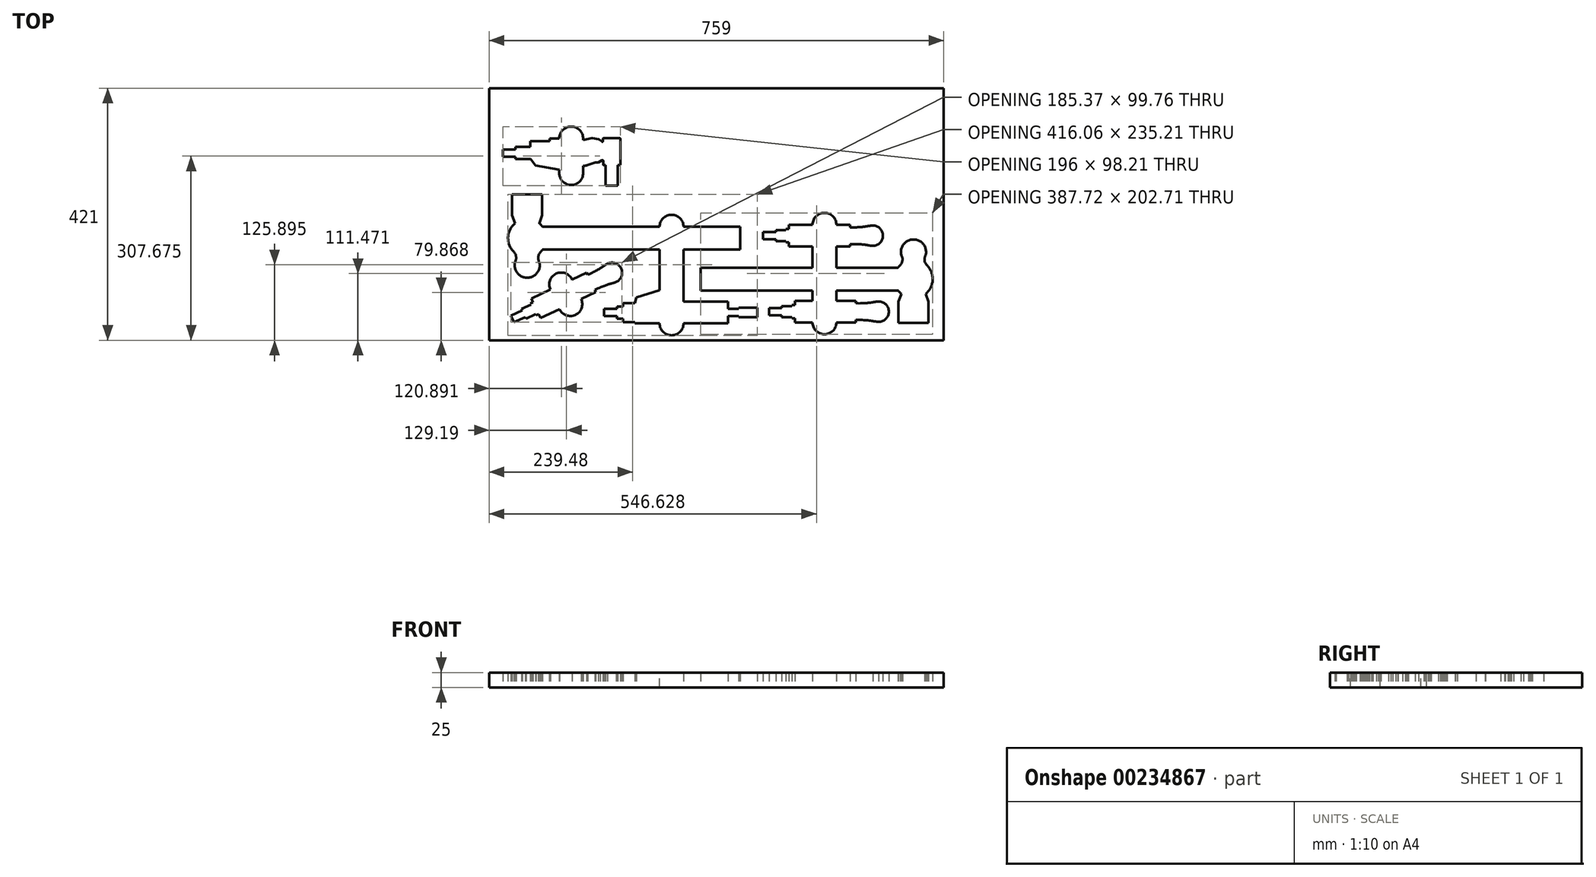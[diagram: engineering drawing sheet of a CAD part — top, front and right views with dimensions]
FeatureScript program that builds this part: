
annotation { "Feature Type Name" : "Feature", "Feature Type Description" : "" }
export const myFeature = defineFeature(function(context is Context, id is Id, definition is map)
    precondition{}
    {
        {
            var Q0;
            Q0=qCreatedBy(makeId("Top.planeOp"),FACE);
            var sketch = newSketch(context, id + "F0", { "sketchPlane" : qUnion([Q0])});
            skLineSegment(sketch, "E0.bottom", {"start": v(0, 0) * mm, "end": v(759, 0) * mm});
            skLineSegment(sketch, "E0.top", {"start": v(0, 421) * mm, "end": v(759, 421) * mm});
            skLineSegment(sketch, "E0.left", {"start": v(0, 0) * mm, "end": v(0, 421) * mm});
            skLineSegment(sketch, "E0.right", {"start": v(759, 0) * mm, "end": v(759, 421) * mm});
            skLineSegment(sketch, "E1", {"start": v(352.77, 83.32) * mm, "end": v(682.77, 83.32) * mm});
            skLineSegment(sketch, "E2", {"start": v(352.77, 83.32) * mm, "end": v(352.77, 121.32) * mm});
            skLineSegment(sketch, "E3", {"start": v(352.77, 121.32) * mm, "end": v(682.77, 121.32) * mm});
            skCircle(sketch, "E4", {"center": v(708.52, 102.32) * mm, "radius": 32 * mm, "construction": true});
            skPoint(sketch, "E4.third.point", {"position": v(740.52, 102.32) * mm});
            skArc(sketch, "E5", {"start": v(728.91, 142.32) * mm, "mid": v(708.52, 168.32) * mm, "end": v(688.12, 142.32) * mm, "construction": true});
            skArc(sketch, "E6", {"start": v(688.12, 142.32) * mm, "mid": v(690.06, 133.5) * mm, "end": v(686.27, 125.32) * mm});
            skArc(sketch, "E7", {"start": v(728.91, 142.32) * mm, "mid": v(726.97, 133.5) * mm, "end": v(730.77, 125.32) * mm});
            skArc(sketch, "E8", {"start": v(688.12, 142.32) * mm, "mid": v(708.52, 168.32) * mm, "end": v(728.91, 142.32) * mm});
            skArc(sketch, "E9", {"start": v(682.77, 121.32) * mm, "mid": v(684.43, 123.4) * mm, "end": v(686.27, 125.32) * mm});
            skArc(sketch, "E10", {"start": v(730.77, 125.32) * mm, "mid": v(740.52, 102.32) * mm, "end": v(730.77, 79.32) * mm});
            skLineSegment(sketch, "E11", {"start": v(688.31, 77.5) * mm, "end": v(683.52, 64.32) * mm});
            skLineSegment(sketch, "E12", {"start": v(728.72, 77.5) * mm, "end": v(733.52, 64.32) * mm});
            skLineSegment(sketch, "E13", {"start": v(733.52, 64.32) * mm, "end": v(733.52, 29.32) * mm});
            skLineSegment(sketch, "E14", {"start": v(733.52, 29.32) * mm, "end": v(683.52, 29.32) * mm});
            skLineSegment(sketch, "E15", {"start": v(683.52, 29.32) * mm, "end": v(683.52, 64.32) * mm});
            skLineSegment(sketch, "E16", {"start": v(683.52, 64.32) * mm, "end": v(733.52, 64.32) * mm, "construction": true});
            skArc(sketch, "E17", {"start": v(682.77, 83.32) * mm, "mid": v(685.36, 80.24) * mm, "end": v(688.31, 77.5) * mm});
            skArc(sketch, "E18", {"start": v(728.72, 77.5) * mm, "mid": v(729.76, 78.39) * mm, "end": v(730.77, 79.32) * mm});
            skLineSegment(sketch, "E19", {"start": v(419.17, 189.5) * mm, "end": v(89.17, 189.5) * mm});
            skLineSegment(sketch, "E20", {"start": v(419.17, 189.5) * mm, "end": v(419.17, 151.5) * mm});
            skLineSegment(sketch, "E21", {"start": v(419.17, 151.5) * mm, "end": v(89.17, 151.5) * mm});
            skCircle(sketch, "E22", {"center": v(63.42, 170.5) * mm, "radius": 32 * mm, "construction": true});
            skPoint(sketch, "E22.third.point", {"position": v(31.42, 170.5) * mm});
            skArc(sketch, "E23", {"start": v(43.02, 130.5) * mm, "mid": v(63.42, 104.5) * mm, "end": v(83.82, 130.5) * mm, "construction": true});
            skArc(sketch, "E24", {"start": v(83.82, 130.5) * mm, "mid": v(81.88, 139.31) * mm, "end": v(85.67, 147.5) * mm});
            skArc(sketch, "E25", {"start": v(43.02, 130.5) * mm, "mid": v(44.96, 139.31) * mm, "end": v(41.17, 147.5) * mm});
            skArc(sketch, "E26", {"start": v(83.82, 130.5) * mm, "mid": v(63.42, 104.5) * mm, "end": v(43.02, 130.5) * mm});
            skArc(sketch, "E27", {"start": v(89.17, 151.5) * mm, "mid": v(87.5, 149.43) * mm, "end": v(85.67, 147.5) * mm});
            skArc(sketch, "E28", {"start": v(41.17, 147.5) * mm, "mid": v(31.42, 170.5) * mm, "end": v(41.17, 193.5) * mm});
            skLineSegment(sketch, "E29", {"start": v(83.62, 195.32) * mm, "end": v(88.42, 208.5) * mm});
            skLineSegment(sketch, "E30", {"start": v(43.22, 195.32) * mm, "end": v(38.42, 208.5) * mm});
            skLineSegment(sketch, "E31", {"start": v(38.42, 208.5) * mm, "end": v(38.42, 243.5) * mm});
            skLineSegment(sketch, "E32", {"start": v(38.42, 243.5) * mm, "end": v(88.42, 243.5) * mm});
            skLineSegment(sketch, "E33", {"start": v(88.42, 243.5) * mm, "end": v(88.42, 208.5) * mm});
            skLineSegment(sketch, "E34", {"start": v(88.42, 208.5) * mm, "end": v(38.42, 208.5) * mm, "construction": true});
            skArc(sketch, "E35", {"start": v(89.17, 189.5) * mm, "mid": v(86.58, 192.58) * mm, "end": v(83.62, 195.32) * mm});
            skArc(sketch, "E36", {"start": v(43.22, 195.32) * mm, "mid": v(42.18, 194.43) * mm, "end": v(41.17, 193.5) * mm});
            skLineSegment(sketch, "E37", {"start": v(467.27, 47.8) * mm, "end": v(650.27, 47.8) * mm, "construction": true});
            skLineSegment(sketch, "E38", {"start": v(467.27, 47.8) * mm, "end": v(467.27, 41.8) * mm});
            skLineSegment(sketch, "E39", {"start": v(467.27, 41.8) * mm, "end": v(488.27, 41.8) * mm});
            skLineSegment(sketch, "E40", {"start": v(488.27, 41.8) * mm, "end": v(488.27, 38.8) * mm});
            skLineSegment(sketch, "E41", {"start": v(488.27, 38.8) * mm, "end": v(505.27, 38.8) * mm});
            skLineSegment(sketch, "E42", {"start": v(505.27, 38.8) * mm, "end": v(505.27, 36.8) * mm});
            skLineSegment(sketch, "E43", {"start": v(505.27, 36.8) * mm, "end": v(510.27, 36.8) * mm});
            skLineSegment(sketch, "E44", {"start": v(510.27, 36.8) * mm, "end": v(510.27, 29.8) * mm});
            skLineSegment(sketch, "E45", {"start": v(510.27, 29.8) * mm, "end": v(612.27, 29.8) * mm});
            skLineSegment(sketch, "E46", {"start": v(612.27, 29.8) * mm, "end": v(612.27, 33.8) * mm});
            skFitSpline(sketch, "E47", {"points": [v(612.27, 33.8) * mm, v(650.27, 30.8) * mm], "startDerivative": vector(70.31, 1.78) * mm, "endDerivative": vector(28.37, -1.58) * mm});
            skArc(sketch, "E48", {"start": v(650.27, 30.8) * mm, "mid": v(667.27, 47.8) * mm, "end": v(650.27, 64.8) * mm});
            skLineSegment(sketch, "E49.MirrorCS", {"start": v(510.27, 65.8) * mm, "end": v(612.27, 65.8) * mm});
            skLineSegment(sketch, "E50.MirrorCS", {"start": v(612.27, 65.8) * mm, "end": v(612.27, 61.8) * mm});
            skFitSpline(sketch, "E51.MirrorCS", {"points": [v(612.27, 61.8) * mm, v(650.27, 64.8) * mm], "startDerivative": vector(70.31, -1.78) * mm, "endDerivative": vector(28.37, 1.58) * mm});
            skLineSegment(sketch, "E52.MirrorCS", {"start": v(505.27, 58.8) * mm, "end": v(510.27, 58.8) * mm});
            skLineSegment(sketch, "E53.MirrorCS", {"start": v(510.27, 58.8) * mm, "end": v(510.27, 65.8) * mm});
            skLineSegment(sketch, "E54.MirrorCS", {"start": v(488.27, 56.8) * mm, "end": v(505.27, 56.8) * mm});
            skLineSegment(sketch, "E55.MirrorCS", {"start": v(505.27, 56.8) * mm, "end": v(505.27, 58.8) * mm});
            skLineSegment(sketch, "E56.MirrorCS", {"start": v(488.27, 53.8) * mm, "end": v(488.27, 56.8) * mm});
            skLineSegment(sketch, "E57.MirrorCS", {"start": v(467.27, 53.8) * mm, "end": v(488.27, 53.8) * mm});
            skLineSegment(sketch, "E58.MirrorCS", {"start": v(467.27, 47.8) * mm, "end": v(467.27, 53.8) * mm});
            skLineSegment(sketch, "E59", {"start": v(39.04, 35.43) * mm, "end": v(204.9, 112.76) * mm, "construction": true});
            skLineSegment(sketch, "E60", {"start": v(39.04, 35.43) * mm, "end": v(41.57, 29.99) * mm});
            skLineSegment(sketch, "E61", {"start": v(41.57, 29.99) * mm, "end": v(60.6, 38.86) * mm});
            skLineSegment(sketch, "E62", {"start": v(60.6, 38.86) * mm, "end": v(61.87, 36.14) * mm});
            skLineSegment(sketch, "E63", {"start": v(61.87, 36.14) * mm, "end": v(77.28, 43.33) * mm});
            skLineSegment(sketch, "E64", {"start": v(77.28, 43.33) * mm, "end": v(78.13, 41.52) * mm});
            skLineSegment(sketch, "E65", {"start": v(78.13, 41.52) * mm, "end": v(82.66, 43.63) * mm});
            skLineSegment(sketch, "E66", {"start": v(82.66, 43.63) * mm, "end": v(85.62, 37.28) * mm});
            skLineSegment(sketch, "E67", {"start": v(85.62, 37.28) * mm, "end": v(178.06, 80.4) * mm});
            skLineSegment(sketch, "E68", {"start": v(178.06, 80.4) * mm, "end": v(176.37, 84.02) * mm});
            skFitSpline(sketch, "E69", {"points": [v(176.37, 84.02) * mm, v(212.08, 97.36) * mm], "startDerivative": vector(62.97, 31.33) * mm, "endDerivative": vector(26.38, 10.56) * mm});
            skArc(sketch, "E70", {"start": v(212.08, 97.36) * mm, "mid": v(220.3, 119.95) * mm, "end": v(197.7, 128.17) * mm});
            skLineSegment(sketch, "E71.MirrorCS", {"start": v(70.4, 69.91) * mm, "end": v(162.85, 113.02) * mm});
            skLineSegment(sketch, "E72.MirrorCS", {"start": v(162.85, 113.02) * mm, "end": v(164.54, 109.4) * mm});
            skFitSpline(sketch, "E73.MirrorCS", {"points": [v(164.54, 109.4) * mm, v(197.7, 128.17) * mm], "startDerivative": vector(64.48, 28.1) * mm, "endDerivative": vector(25.04, 13.42) * mm});
            skLineSegment(sketch, "E74.MirrorCS", {"start": v(68.83, 61.45) * mm, "end": v(73.36, 63.57) * mm});
            skLineSegment(sketch, "E75.MirrorCS", {"start": v(73.36, 63.57) * mm, "end": v(70.4, 69.91) * mm});
            skLineSegment(sketch, "E76.MirrorCS", {"start": v(54.27, 52.46) * mm, "end": v(69.67, 59.64) * mm});
            skLineSegment(sketch, "E77.MirrorCS", {"start": v(69.67, 59.64) * mm, "end": v(68.83, 61.45) * mm});
            skLineSegment(sketch, "E78.MirrorCS", {"start": v(55.54, 49.74) * mm, "end": v(54.27, 52.46) * mm});
            skLineSegment(sketch, "E79.MirrorCS", {"start": v(36.5, 40.86) * mm, "end": v(55.54, 49.74) * mm});
            skLineSegment(sketch, "E80.MirrorCS", {"start": v(39.04, 35.43) * mm, "end": v(36.5, 40.86) * mm});
            skLineSegment(sketch, "E81", {"start": v(457.5, 174.7) * mm, "end": v(640.5, 174.7) * mm, "construction": true});
            skLineSegment(sketch, "E82", {"start": v(457.5, 174.7) * mm, "end": v(457.5, 168.7) * mm});
            skLineSegment(sketch, "E83", {"start": v(457.5, 168.7) * mm, "end": v(478.5, 168.7) * mm});
            skLineSegment(sketch, "E84", {"start": v(478.5, 168.7) * mm, "end": v(478.5, 165.7) * mm});
            skLineSegment(sketch, "E85", {"start": v(478.5, 165.7) * mm, "end": v(495.5, 165.7) * mm});
            skLineSegment(sketch, "E86", {"start": v(495.5, 165.7) * mm, "end": v(495.5, 163.7) * mm});
            skLineSegment(sketch, "E87", {"start": v(495.5, 163.7) * mm, "end": v(500.5, 163.7) * mm});
            skLineSegment(sketch, "E88", {"start": v(500.5, 163.7) * mm, "end": v(500.5, 156.7) * mm});
            skLineSegment(sketch, "E89", {"start": v(500.5, 156.7) * mm, "end": v(602.5, 156.7) * mm});
            skLineSegment(sketch, "E90", {"start": v(602.5, 156.7) * mm, "end": v(602.5, 160.7) * mm});
            skFitSpline(sketch, "E91", {"points": [v(602.5, 160.7) * mm, v(640.5, 157.7) * mm], "startDerivative": vector(70.31, 1.78) * mm, "endDerivative": vector(28.37, -1.58) * mm});
            skArc(sketch, "E92", {"start": v(640.5, 157.7) * mm, "mid": v(657.5, 174.7) * mm, "end": v(640.5, 191.7) * mm});
            skLineSegment(sketch, "E93.MirrorCS", {"start": v(500.5, 192.7) * mm, "end": v(602.5, 192.7) * mm});
            skLineSegment(sketch, "E94.MirrorCS", {"start": v(602.5, 192.7) * mm, "end": v(602.5, 188.7) * mm});
            skFitSpline(sketch, "E95.MirrorCS", {"points": [v(602.5, 188.7) * mm, v(640.5, 191.7) * mm], "startDerivative": vector(70.31, -1.78) * mm, "endDerivative": vector(28.37, 1.58) * mm});
            skLineSegment(sketch, "E96.MirrorCS", {"start": v(495.5, 185.7) * mm, "end": v(500.5, 185.7) * mm});
            skLineSegment(sketch, "E97.MirrorCS", {"start": v(500.5, 185.7) * mm, "end": v(500.5, 192.7) * mm});
            skLineSegment(sketch, "E98.MirrorCS", {"start": v(478.5, 183.7) * mm, "end": v(495.5, 183.7) * mm});
            skLineSegment(sketch, "E99.MirrorCS", {"start": v(495.5, 183.7) * mm, "end": v(495.5, 185.7) * mm});
            skLineSegment(sketch, "E100.MirrorCS", {"start": v(478.5, 180.7) * mm, "end": v(478.5, 183.7) * mm});
            skLineSegment(sketch, "E101.MirrorCS", {"start": v(457.5, 180.7) * mm, "end": v(478.5, 180.7) * mm});
            skLineSegment(sketch, "E102.MirrorCS", {"start": v(457.5, 174.7) * mm, "end": v(457.5, 180.7) * mm});
            skLineSegment(sketch, "E103", {"start": v(191.5, 46.29) * mm, "end": v(447.5, 46.29) * mm, "construction": true});
            skLineSegment(sketch, "E104", {"start": v(191.5, 46.29) * mm, "end": v(191.5, 40.29) * mm});
            skLineSegment(sketch, "E105", {"start": v(191.5, 40.29) * mm, "end": v(213.5, 40.29) * mm});
            skLineSegment(sketch, "E106", {"start": v(213.5, 40.29) * mm, "end": v(213.5, 36.29) * mm});
            skLineSegment(sketch, "E107", {"start": v(213.5, 36.29) * mm, "end": v(223.5, 36.29) * mm});
            skLineSegment(sketch, "E108", {"start": v(223.5, 36.29) * mm, "end": v(223.5, 30.29) * mm});
            skLineSegment(sketch, "E109", {"start": v(223.5, 30.29) * mm, "end": v(243.5, 30.29) * mm});
            skLineSegment(sketch, "E110", {"start": v(243.5, 30.29) * mm, "end": v(243.5, 28.29) * mm});
            skLineSegment(sketch, "E111", {"start": v(243.5, 28.29) * mm, "end": v(398.5, 28.29) * mm});
            skLineSegment(sketch, "E112", {"start": v(398.5, 28.29) * mm, "end": v(398.5, 40.29) * mm});
            skLineSegment(sketch, "E113", {"start": v(398.5, 40.29) * mm, "end": v(416.5, 40.29) * mm});
            skLineSegment(sketch, "E114", {"start": v(416.5, 40.29) * mm, "end": v(416.5, 38.29) * mm});
            skLineSegment(sketch, "E115", {"start": v(416.5, 38.29) * mm, "end": v(447.5, 38.29) * mm});
            skLineSegment(sketch, "E116", {"start": v(447.5, 38.29) * mm, "end": v(447.5, 46.29) * mm});
            skLineSegment(sketch, "E117.MirrorCS", {"start": v(191.5, 46.29) * mm, "end": v(191.5, 52.29) * mm});
            skLineSegment(sketch, "E118.MirrorCS", {"start": v(191.5, 52.29) * mm, "end": v(213.5, 52.29) * mm});
            skLineSegment(sketch, "E119.MirrorCS", {"start": v(213.5, 52.29) * mm, "end": v(213.5, 56.29) * mm});
            skLineSegment(sketch, "E120.MirrorCS", {"start": v(213.5, 56.29) * mm, "end": v(223.5, 56.29) * mm});
            skLineSegment(sketch, "E121.MirrorCS", {"start": v(223.5, 56.29) * mm, "end": v(223.5, 62.29) * mm});
            skLineSegment(sketch, "E122.MirrorCS", {"start": v(223.5, 62.29) * mm, "end": v(243.5, 62.29) * mm});
            skLineSegment(sketch, "E123.MirrorCS", {"start": v(398.5, 64.29) * mm, "end": v(398.5, 52.29) * mm});
            skLineSegment(sketch, "E124.MirrorCS", {"start": v(398.5, 52.29) * mm, "end": v(416.5, 52.29) * mm});
            skLineSegment(sketch, "E125.MirrorCS", {"start": v(416.5, 52.29) * mm, "end": v(416.5, 54.29) * mm});
            skLineSegment(sketch, "E126.MirrorCS", {"start": v(416.5, 54.29) * mm, "end": v(447.5, 54.29) * mm});
            skLineSegment(sketch, "E127.MirrorCS", {"start": v(447.5, 54.29) * mm, "end": v(447.5, 46.29) * mm});
            skLineSegment(sketch, "E128", {"start": v(398.5, 64.29) * mm, "end": v(324.5, 64.29) * mm});
            skLineSegment(sketch, "E129", {"start": v(324.5, 64.29) * mm, "end": v(324.5, 88.29) * mm});
            skLineSegment(sketch, "E130", {"start": v(324.5, 88.29) * mm, "end": v(300.5, 88.29) * mm});
            skLineSegment(sketch, "E131", {"start": v(300.5, 88.29) * mm, "end": v(245.93, 71.6) * mm});
            skLineSegment(sketch, "E132", {"start": v(245.93, 71.6) * mm, "end": v(243.5, 62.29) * mm});
            skLineSegment(sketch, "E133.0", {"start": v(204.9, 112.76) * mm, "end": v(197.7, 128.17) * mm, "construction": true});
            skLineSegment(sketch, "E134", {"start": v(22.9, 312.78) * mm, "end": v(218.9, 312.78) * mm, "construction": true});
            skLineSegment(sketch, "E135", {"start": v(22.9, 312.78) * mm, "end": v(22.9, 318.78) * mm});
            skLineSegment(sketch, "E136", {"start": v(22.9, 318.78) * mm, "end": v(43.9, 318.78) * mm});
            skLineSegment(sketch, "E137", {"start": v(43.9, 318.78) * mm, "end": v(43.9, 322.78) * mm});
            skLineSegment(sketch, "E138", {"start": v(43.9, 322.78) * mm, "end": v(68.9, 322.78) * mm});
            skLineSegment(sketch, "E139", {"start": v(68.9, 322.78) * mm, "end": v(68.9, 332.78) * mm});
            skLineSegment(sketch, "E140", {"start": v(68.9, 332.78) * mm, "end": v(100.9, 332.78) * mm});
            skLineSegment(sketch, "E141", {"start": v(100.9, 332.78) * mm, "end": v(100.9, 336.78) * mm});
            skLineSegment(sketch, "E142", {"start": v(100.9, 336.78) * mm, "end": v(124.9, 336.78) * mm});
            skLineSegment(sketch, "E143", {"start": v(124.9, 336.78) * mm, "end": v(124.9, 332.78) * mm});
            skLineSegment(sketch, "E144", {"start": v(124.9, 332.78) * mm, "end": v(146.9, 332.78) * mm});
            skLineSegment(sketch, "E145", {"start": v(146.9, 332.78) * mm, "end": v(171.72, 337.53) * mm});
            skLineSegment(sketch, "E146", {"start": v(190.9, 337.57) * mm, "end": v(217.9, 337.57) * mm});
            skLineSegment(sketch, "E147", {"start": v(218.9, 336.57) * mm, "end": v(218.9, 293.57) * mm});
            skLineSegment(sketch, "E148", {"start": v(189.9, 336.57) * mm, "end": v(189.9, 332.55) * mm});
            skLineSegment(sketch, "E149", {"start": v(188.3, 331.75) * mm, "end": v(183.08, 335.59) * mm});
            skLineSegment(sketch, "E150", {"start": v(182.66, 335.77) * mm, "end": v(172.07, 337.54) * mm});
            skPoint(sketch, "E151.visualSharp", {"position": v(189.9, 330.57) * mm});
            skArc(sketch, "E151.filletArc", {"start": v(188.3, 331.75) * mm, "mid": v(189.34, 331.66) * mm, "end": v(189.9, 332.55) * mm});
            skPoint(sketch, "E152.visualSharp", {"position": v(189.9, 337.57) * mm});
            skArc(sketch, "E152.filletArc", {"start": v(190.9, 337.57) * mm, "mid": v(190.18, 337.28) * mm, "end": v(189.9, 336.57) * mm});
            skPoint(sketch, "E153.visualSharp", {"position": v(218.9, 337.57) * mm});
            skArc(sketch, "E153.filletArc", {"start": v(218.9, 336.57) * mm, "mid": v(218.6, 337.28) * mm, "end": v(217.9, 337.57) * mm});
            skPoint(sketch, "E154.visualSharp", {"position": v(171.9, 337.57) * mm});
            skArc(sketch, "E154.filletArc", {"start": v(172.07, 337.54) * mm, "mid": v(171.9, 337.55) * mm, "end": v(171.72, 337.53) * mm});
            skPoint(sketch, "E155.visualSharp", {"position": v(182.9, 335.73) * mm});
            skArc(sketch, "E155.filletArc", {"start": v(183.08, 335.59) * mm, "mid": v(182.88, 335.7) * mm, "end": v(182.66, 335.77) * mm});
            skLineSegment(sketch, "E156", {"start": v(124.9, 332.78) * mm, "end": v(100.9, 332.78) * mm, "construction": true});
            skLineSegment(sketch, "E157.MirrorCS", {"start": v(43.9, 302.78) * mm, "end": v(68.4, 302.78) * mm});
            skLineSegment(sketch, "E158.MirrorCS", {"start": v(43.9, 306.78) * mm, "end": v(43.9, 302.78) * mm});
            skLineSegment(sketch, "E159.MirrorCS", {"start": v(22.9, 312.78) * mm, "end": v(22.9, 306.78) * mm});
            skLineSegment(sketch, "E160.MirrorCS", {"start": v(22.9, 306.78) * mm, "end": v(43.9, 306.78) * mm});
            skLineSegment(sketch, "E161", {"start": v(69.2, 302.4) * mm, "end": v(77.14, 292.33) * mm});
            skLineSegment(sketch, "E162", {"start": v(77.75, 291.97) * mm, "end": v(134.96, 281.8) * mm});
            skArc(sketch, "E163", {"start": v(135.56, 280.18) * mm, "mid": v(138, 272.67) * mm, "end": v(143.7, 278.13) * mm});
            skLineSegment(sketch, "E164", {"start": v(144.69, 279.33) * mm, "end": v(155.37, 279.33) * mm});
            skLineSegment(sketch, "E165", {"start": v(156.28, 280.74) * mm, "end": v(152.07, 289.96) * mm});
            skArc(sketch, "E166", {"start": v(153.09, 291.37) * mm, "mid": v(158.59, 291.34) * mm, "end": v(163.97, 292.46) * mm});
            skLineSegment(sketch, "E167", {"start": v(163.97, 292.46) * mm, "end": v(177.3, 296.7) * mm});
            skLineSegment(sketch, "E168", {"start": v(177.3, 296.7) * mm, "end": v(182.19, 296.7) * mm});
            skLineSegment(sketch, "E169", {"start": v(182.19, 296.7) * mm, "end": v(185.45, 299.03) * mm});
            skLineSegment(sketch, "E170", {"start": v(185.45, 299.03) * mm, "end": v(188.84, 300.54) * mm});
            skLineSegment(sketch, "E171", {"start": v(190.25, 299.63) * mm, "end": v(190.25, 293.57) * mm});
            skLineSegment(sketch, "E172", {"start": v(214.9, 292.57) * mm, "end": v(217.9, 292.57) * mm});
            skLineSegment(sketch, "E173", {"start": v(204.57, 258.57) * mm, "end": v(204.57, 337.57) * mm, "construction": true});
            skLineSegment(sketch, "E174", {"start": v(214.9, 292.57) * mm, "end": v(214.9, 258.57) * mm});
            skLineSegment(sketch, "E175", {"start": v(214.9, 258.57) * mm, "end": v(204.57, 258.57) * mm});
            skLineSegment(sketch, "E176.MirrorCS", {"start": v(194.25, 292.57) * mm, "end": v(194.25, 258.57) * mm});
            skLineSegment(sketch, "E177.MirrorCS", {"start": v(194.25, 258.57) * mm, "end": v(204.57, 258.57) * mm});
            skLineSegment(sketch, "E178.MirrorCS", {"start": v(194.25, 292.57) * mm, "end": v(191.25, 292.57) * mm});
            skPoint(sketch, "E179.visualSharp", {"position": v(190.25, 301.16) * mm});
            skArc(sketch, "E179.filletArc", {"start": v(190.25, 299.63) * mm, "mid": v(189.8, 300.46) * mm, "end": v(188.84, 300.54) * mm});
            skPoint(sketch, "E180.visualSharp", {"position": v(190.25, 292.57) * mm});
            skArc(sketch, "E180.filletArc", {"start": v(190.25, 293.57) * mm, "mid": v(190.54, 292.86) * mm, "end": v(191.25, 292.57) * mm});
            skPoint(sketch, "E181.visualSharp", {"position": v(218.9, 292.57) * mm});
            skArc(sketch, "E181.filletArc", {"start": v(217.9, 292.57) * mm, "mid": v(218.6, 292.86) * mm, "end": v(218.9, 293.57) * mm});
            skPoint(sketch, "E182.visualSharp", {"position": v(137.16, 281.41) * mm});
            skArc(sketch, "E182.filletArc", {"start": v(135.56, 280.18) * mm, "mid": v(135.73, 281.16) * mm, "end": v(134.96, 281.8) * mm});
            skPoint(sketch, "E183.visualSharp", {"position": v(143.29, 279.33) * mm});
            skArc(sketch, "E183.filletArc", {"start": v(144.69, 279.33) * mm, "mid": v(143.91, 278.96) * mm, "end": v(143.7, 278.13) * mm});
            skPoint(sketch, "E184.visualSharp", {"position": v(156.92, 279.33) * mm});
            skArc(sketch, "E184.filletArc", {"start": v(155.37, 279.33) * mm, "mid": v(156.2, 279.79) * mm, "end": v(156.28, 280.74) * mm});
            skPoint(sketch, "E185.visualSharp", {"position": v(151.3, 291.63) * mm});
            skArc(sketch, "E185.filletArc", {"start": v(153.09, 291.37) * mm, "mid": v(152.17, 290.97) * mm, "end": v(152.07, 289.96) * mm});
            skPoint(sketch, "E186.visualSharp", {"position": v(77.38, 292.03) * mm});
            skArc(sketch, "E186.filletArc", {"start": v(77.14, 292.33) * mm, "mid": v(77.41, 292.1) * mm, "end": v(77.75, 291.97) * mm});
            skPoint(sketch, "E187.visualSharp", {"position": v(68.9, 302.78) * mm});
            skArc(sketch, "E187.filletArc", {"start": v(69.2, 302.4) * mm, "mid": v(68.84, 302.68) * mm, "end": v(68.4, 302.78) * mm});
            skSolve(sketch);
        }
        {
            var Q0;
            Q0 = qSketchRegion(id + "F0", true);
            extrude(context, id + "F1", {"entities" : qUnion([Q0]), "depth" : 25 * mm});
        }
        {
            var Q0;
            Q0=qCreatedBy(makeId("Top.planeOp"),FACE);
            var sketch = newSketch(context, id + "F2", { "sketchPlane" : qUnion([Q0])});
            skLineSegment(sketch, "E188.left", {"start": v(539.87, 192.83) * mm, "end": v(539.87, 30.12) * mm});
            skLineSegment(sketch, "E188.right", {"start": v(579.87, 192.83) * mm, "end": v(579.87, 30.12) * mm});
            skArc(sketch, "E189", {"start": v(539.87, 192.83) * mm, "mid": v(559.87, 212.83) * mm, "end": v(579.87, 192.83) * mm});
            skArc(sketch, "E190", {"start": v(579.87, 30.12) * mm, "mid": v(559.87, 10.12) * mm, "end": v(539.87, 30.12) * mm});
            skLineSegment(sketch, "E191", {"start": v(138.37, 101.6) * mm, "end": v(153.58, 68.98) * mm, "construction": true});
            skLineSegment(sketch, "E192", {"start": v(138.37, 101.6) * mm, "end": v(102.12, 84.7) * mm, "construction": true});
            skLineSegment(sketch, "E193", {"start": v(102.12, 84.7) * mm, "end": v(117.33, 52.07) * mm, "construction": true});
            skLineSegment(sketch, "E194", {"start": v(117.33, 52.07) * mm, "end": v(153.58, 68.98) * mm, "construction": true});
            skLineSegment(sketch, "E195", {"start": v(102.12, 84.7) * mm, "end": v(117.33, 52.07) * mm});
            skLineSegment(sketch, "E196", {"start": v(138.37, 101.6) * mm, "end": v(153.58, 68.98) * mm});
            skArc(sketch, "E197", {"start": v(138.37, 101.6) * mm, "mid": v(111.8, 111.28) * mm, "end": v(102.12, 84.7) * mm});
            skArc(sketch, "E198", {"start": v(117.33, 52.07) * mm, "mid": v(143.91, 42.4) * mm, "end": v(153.58, 68.98) * mm});
            skLineSegment(sketch, "E199.left", {"start": v(284.5, 189.5) * mm, "end": v(284.5, 28.29) * mm});
            skLineSegment(sketch, "E199.right", {"start": v(324.5, 189.5) * mm, "end": v(324.5, 28.29) * mm});
            skArc(sketch, "E200", {"start": v(284.5, 189.5) * mm, "mid": v(304.5, 209.5) * mm, "end": v(324.5, 189.5) * mm});
            skArc(sketch, "E201", {"start": v(324.5, 28.29) * mm, "mid": v(304.5, 8.29) * mm, "end": v(284.5, 28.29) * mm});
            skLineSegment(sketch, "E202.left", {"start": v(116.92, 336.78) * mm, "end": v(116.92, 279.33) * mm});
            skLineSegment(sketch, "E202.right", {"start": v(156.92, 336.78) * mm, "end": v(156.92, 279.33) * mm});
            skArc(sketch, "E203", {"start": v(116.92, 336.78) * mm, "mid": v(136.92, 356.78) * mm, "end": v(156.92, 336.78) * mm});
            skArc(sketch, "E204", {"start": v(156.92, 279.33) * mm, "mid": v(136.92, 259.33) * mm, "end": v(116.92, 279.33) * mm});
            skLineSegment(sketch, "E205", {"start": v(156.92, 279.33) * mm, "end": v(116.92, 279.33) * mm, "construction": true});
            skLineSegment(sketch, "E206", {"start": v(0, 0) * mm, "end": v(150, 0) * mm, "construction": true});
            skSolve(sketch);
        }
        {
            var Q0;
            Q0 = qSketchRegion(id + "F2", true);
            extrude(context, id + "F3", {"entities" : qUnion([Q0]), "operationType" : NewBodyOperationType.REMOVE, "depth" : 25 * mm});
        }
    });
